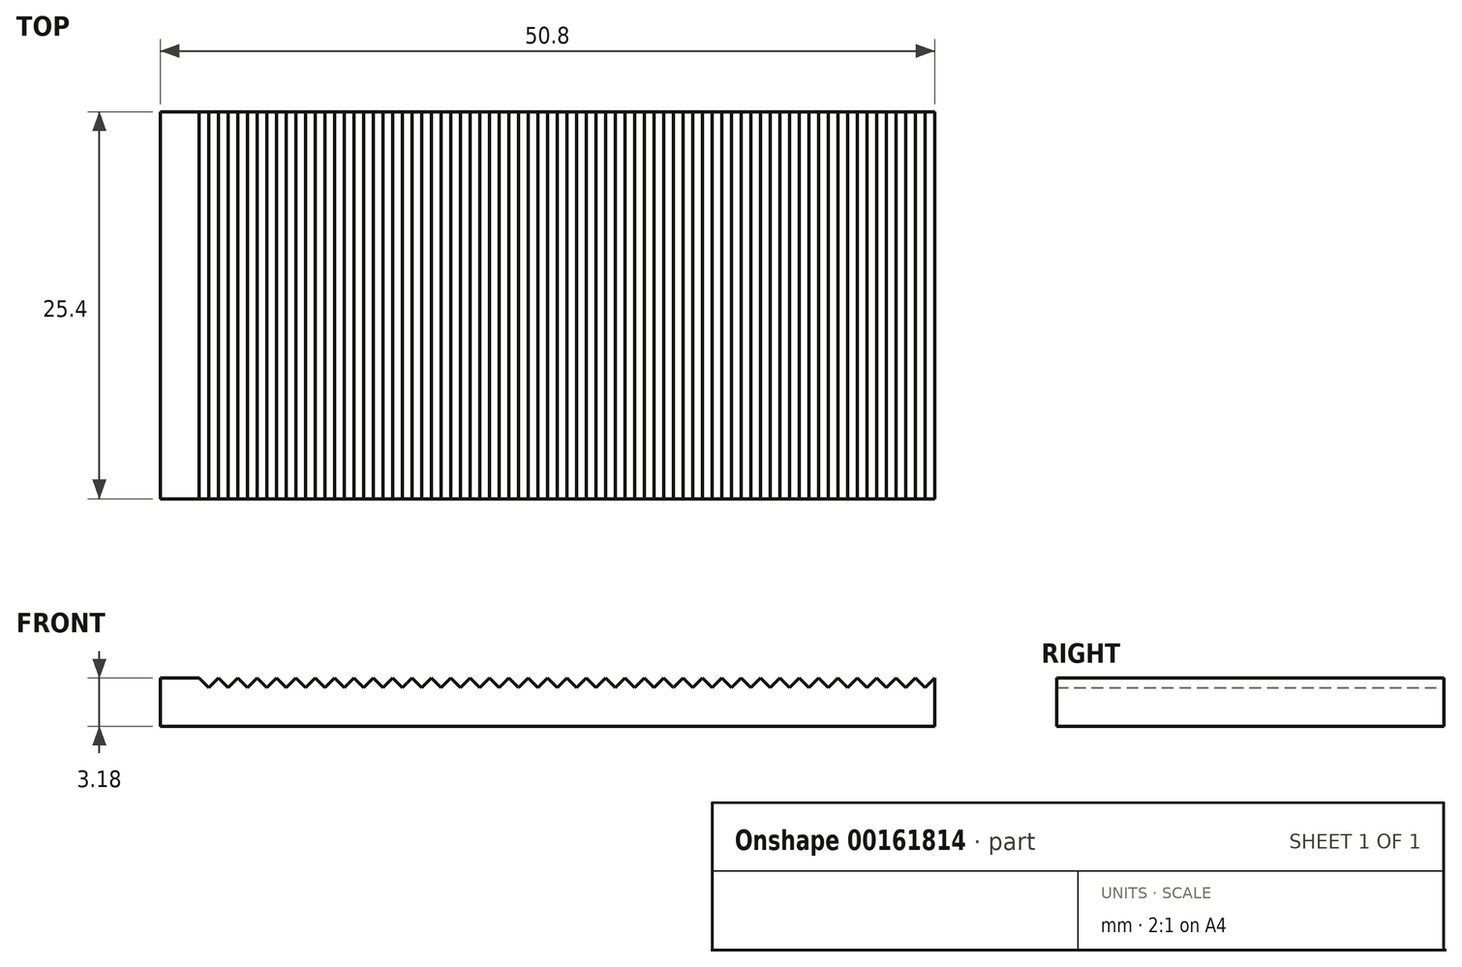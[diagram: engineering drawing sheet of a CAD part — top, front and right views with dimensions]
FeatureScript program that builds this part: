
annotation { "Feature Type Name" : "Feature", "Feature Type Description" : "" }
export const myFeature = defineFeature(function(context is Context, id is Id, definition is map)
    precondition{}
    {
        {
            var Q0;
            Q0=qCreatedBy(makeId("Front.planeOp"), FACE);
            var sketch = newSketch(context, id + "F0", { "sketchPlane" : qUnion([Q0])});
            skLineSegment(sketch, "E0", {"start": v(0, 0) * mm, "end": v(50.8, 0) * mm});
            skLineSegment(sketch, "E1", {"start": v(50.8, 0) * mm, "end": v(50.8, 3.17) * mm});
            skLineSegment(sketch, "E2", {"start": v(50.16, 2.54) * mm, "end": v(49.53, 3.18) * mm});
            skLineSegment(sketch, "E3", {"start": v(50.16, 2.54) * mm, "end": v(50.8, 3.18) * mm});
            skLineSegment(sketch, "E4.1.0.0", {"start": v(48.9, 2.54) * mm, "end": v(49.53, 3.18) * mm});
            skLineSegment(sketch, "E4.1.0.1", {"start": v(48.9, 2.54) * mm, "end": v(48.26, 3.18) * mm});
            skLineSegment(sketch, "E4.2.0.0", {"start": v(47.62, 2.54) * mm, "end": v(48.26, 3.18) * mm});
            skLineSegment(sketch, "E4.2.0.1", {"start": v(47.62, 2.54) * mm, "end": v(47, 3.18) * mm});
            skLineSegment(sketch, "E4.3.0.0", {"start": v(46.35, 2.54) * mm, "end": v(47, 3.18) * mm});
            skLineSegment(sketch, "E4.3.0.1", {"start": v(46.35, 2.54) * mm, "end": v(45.72, 3.18) * mm});
            skLineSegment(sketch, "E4.4.0.0", {"start": v(45.09, 2.54) * mm, "end": v(45.72, 3.18) * mm});
            skLineSegment(sketch, "E4.4.0.1", {"start": v(45.09, 2.54) * mm, "end": v(44.45, 3.18) * mm});
            skLineSegment(sketch, "E4.5.0.0", {"start": v(43.81, 2.54) * mm, "end": v(44.45, 3.18) * mm});
            skLineSegment(sketch, "E4.5.0.1", {"start": v(43.81, 2.54) * mm, "end": v(43.18, 3.18) * mm});
            skLineSegment(sketch, "E4.6.0.0", {"start": v(42.55, 2.54) * mm, "end": v(43.18, 3.18) * mm});
            skLineSegment(sketch, "E4.6.0.1", {"start": v(42.55, 2.54) * mm, "end": v(41.91, 3.18) * mm});
            skLineSegment(sketch, "E4.7.0.0", {"start": v(41.27, 2.54) * mm, "end": v(41.91, 3.18) * mm});
            skLineSegment(sketch, "E4.7.0.1", {"start": v(41.27, 2.54) * mm, "end": v(40.64, 3.18) * mm});
            skLineSegment(sketch, "E4.8.0.0", {"start": v(40, 2.54) * mm, "end": v(40.64, 3.18) * mm});
            skLineSegment(sketch, "E4.8.0.1", {"start": v(40, 2.54) * mm, "end": v(39.37, 3.18) * mm});
            skLineSegment(sketch, "E4.9.0.0", {"start": v(38.73, 2.54) * mm, "end": v(39.37, 3.18) * mm});
            skLineSegment(sketch, "E4.9.0.1", {"start": v(38.73, 2.54) * mm, "end": v(38.1, 3.18) * mm});
            skLineSegment(sketch, "E4.10.0.0", {"start": v(37.46, 2.54) * mm, "end": v(38.1, 3.18) * mm});
            skLineSegment(sketch, "E4.10.0.1", {"start": v(37.46, 2.54) * mm, "end": v(36.83, 3.18) * mm});
            skLineSegment(sketch, "E4.11.0.0", {"start": v(36.2, 2.54) * mm, "end": v(36.83, 3.18) * mm});
            skLineSegment(sketch, "E4.11.0.1", {"start": v(36.2, 2.54) * mm, "end": v(35.56, 3.18) * mm});
            skLineSegment(sketch, "E4.12.0.0", {"start": v(34.92, 2.54) * mm, "end": v(35.56, 3.18) * mm});
            skLineSegment(sketch, "E4.12.0.1", {"start": v(34.92, 2.54) * mm, "end": v(34.3, 3.18) * mm});
            skLineSegment(sketch, "E4.13.0.0", {"start": v(33.65, 2.54) * mm, "end": v(34.3, 3.18) * mm});
            skLineSegment(sketch, "E4.13.0.1", {"start": v(33.65, 2.54) * mm, "end": v(33.02, 3.18) * mm});
            skLineSegment(sketch, "E4.14.0.0", {"start": v(32.38, 2.54) * mm, "end": v(33.02, 3.18) * mm});
            skLineSegment(sketch, "E4.14.0.1", {"start": v(32.38, 2.54) * mm, "end": v(31.75, 3.18) * mm});
            skLineSegment(sketch, "E4.15.0.0", {"start": v(31.11, 2.54) * mm, "end": v(31.75, 3.18) * mm});
            skLineSegment(sketch, "E4.15.0.1", {"start": v(31.11, 2.54) * mm, "end": v(30.48, 3.18) * mm});
            skLineSegment(sketch, "E4.16.0.0", {"start": v(29.84, 2.54) * mm, "end": v(30.48, 3.18) * mm});
            skLineSegment(sketch, "E4.16.0.1", {"start": v(29.84, 2.54) * mm, "end": v(29.21, 3.18) * mm});
            skLineSegment(sketch, "E4.17.0.0", {"start": v(28.57, 2.54) * mm, "end": v(29.21, 3.18) * mm});
            skLineSegment(sketch, "E4.17.0.1", {"start": v(28.57, 2.54) * mm, "end": v(27.94, 3.18) * mm});
            skLineSegment(sketch, "E4.18.0.0", {"start": v(27.3, 2.54) * mm, "end": v(27.94, 3.18) * mm});
            skLineSegment(sketch, "E4.18.0.1", {"start": v(27.3, 2.54) * mm, "end": v(26.67, 3.18) * mm});
            skLineSegment(sketch, "E4.19.0.0", {"start": v(26.03, 2.54) * mm, "end": v(26.67, 3.18) * mm});
            skLineSegment(sketch, "E4.19.0.1", {"start": v(26.03, 2.54) * mm, "end": v(25.4, 3.18) * mm});
            skLineSegment(sketch, "E4.20.0.0", {"start": v(24.76, 2.54) * mm, "end": v(25.4, 3.18) * mm});
            skLineSegment(sketch, "E4.20.0.1", {"start": v(24.76, 2.54) * mm, "end": v(24.13, 3.18) * mm});
            skLineSegment(sketch, "E4.21.0.0", {"start": v(23.5, 2.54) * mm, "end": v(24.13, 3.18) * mm});
            skLineSegment(sketch, "E4.21.0.1", {"start": v(23.5, 2.54) * mm, "end": v(22.86, 3.18) * mm});
            skLineSegment(sketch, "E4.22.0.0", {"start": v(22.22, 2.54) * mm, "end": v(22.86, 3.18) * mm});
            skLineSegment(sketch, "E4.22.0.1", {"start": v(22.22, 2.54) * mm, "end": v(21.6, 3.18) * mm});
            skLineSegment(sketch, "E4.23.0.0", {"start": v(20.95, 2.54) * mm, "end": v(21.59, 3.18) * mm});
            skLineSegment(sketch, "E4.23.0.1", {"start": v(20.95, 2.54) * mm, "end": v(20.32, 3.18) * mm});
            skLineSegment(sketch, "E4.24.0.0", {"start": v(19.68, 2.54) * mm, "end": v(20.32, 3.18) * mm});
            skLineSegment(sketch, "E4.24.0.1", {"start": v(19.68, 2.54) * mm, "end": v(19.05, 3.18) * mm});
            skLineSegment(sketch, "E4.25.0.0", {"start": v(18.41, 2.54) * mm, "end": v(19.05, 3.18) * mm});
            skLineSegment(sketch, "E4.25.0.1", {"start": v(18.41, 2.54) * mm, "end": v(17.78, 3.18) * mm});
            skLineSegment(sketch, "E4.26.0.0", {"start": v(17.14, 2.54) * mm, "end": v(17.78, 3.18) * mm});
            skLineSegment(sketch, "E4.26.0.1", {"start": v(17.14, 2.54) * mm, "end": v(16.51, 3.18) * mm});
            skLineSegment(sketch, "E4.27.0.0", {"start": v(15.87, 2.54) * mm, "end": v(16.5, 3.18) * mm});
            skLineSegment(sketch, "E4.27.0.1", {"start": v(15.87, 2.54) * mm, "end": v(15.24, 3.18) * mm});
            skLineSegment(sketch, "E4.28.0.0", {"start": v(14.6, 2.54) * mm, "end": v(15.24, 3.18) * mm});
            skLineSegment(sketch, "E4.28.0.1", {"start": v(14.6, 2.54) * mm, "end": v(13.97, 3.18) * mm});
            skLineSegment(sketch, "E4.29.0.0", {"start": v(13.33, 2.54) * mm, "end": v(13.97, 3.18) * mm});
            skLineSegment(sketch, "E4.29.0.1", {"start": v(13.33, 2.54) * mm, "end": v(12.7, 3.18) * mm});
            skLineSegment(sketch, "E4.30.0.0", {"start": v(12.06, 2.54) * mm, "end": v(12.7, 3.18) * mm});
            skLineSegment(sketch, "E4.30.0.1", {"start": v(12.06, 2.54) * mm, "end": v(11.43, 3.18) * mm});
            skLineSegment(sketch, "E4.31.0.0", {"start": v(10.8, 2.54) * mm, "end": v(11.43, 3.18) * mm});
            skLineSegment(sketch, "E4.31.0.1", {"start": v(10.8, 2.54) * mm, "end": v(10.16, 3.18) * mm});
            skLineSegment(sketch, "E4.32.0.0", {"start": v(9.52, 2.54) * mm, "end": v(10.16, 3.18) * mm});
            skLineSegment(sketch, "E4.32.0.1", {"start": v(9.52, 2.54) * mm, "end": v(8.89, 3.18) * mm});
            skLineSegment(sketch, "E4.33.0.0", {"start": v(8.25, 2.54) * mm, "end": v(8.89, 3.18) * mm});
            skLineSegment(sketch, "E4.33.0.1", {"start": v(8.25, 2.54) * mm, "end": v(7.62, 3.18) * mm});
            skLineSegment(sketch, "E4.34.0.0", {"start": v(6.98, 2.54) * mm, "end": v(7.62, 3.18) * mm});
            skLineSegment(sketch, "E4.34.0.1", {"start": v(6.98, 2.54) * mm, "end": v(6.35, 3.18) * mm});
            skLineSegment(sketch, "E4.35.0.0", {"start": v(5.71, 2.54) * mm, "end": v(6.35, 3.18) * mm});
            skLineSegment(sketch, "E4.35.0.1", {"start": v(5.71, 2.54) * mm, "end": v(5.08, 3.18) * mm});
            skLineSegment(sketch, "E4.36.0.0", {"start": v(4.44, 2.54) * mm, "end": v(5.08, 3.18) * mm});
            skLineSegment(sketch, "E4.36.0.1", {"start": v(4.44, 2.54) * mm, "end": v(3.8, 3.18) * mm});
            skLineSegment(sketch, "E4.37.0.0", {"start": v(3.17, 2.54) * mm, "end": v(3.8, 3.18) * mm});
            skLineSegment(sketch, "E4.37.0.1", {"start": v(3.17, 2.54) * mm, "end": v(2.54, 3.18) * mm});
            skLineSegment(sketch, "E4.direction1", {"start": v(50.16, 2.54) * mm, "end": v(48.9, 2.54) * mm, "construction": true});
            skLineSegment(sketch, "E5", {"start": v(0, 3.17) * mm, "end": v(2.54, 3.17) * mm});
            skLineSegment(sketch, "E6", {"start": v(0, 3.17) * mm, "end": v(0, 0) * mm});
            skSolve(sketch);
        }
        {
            var Q0;
            Q0 = qSketchRegion(id + "F0", true);
            extrude(context, id + "F1", {"entities" : qUnion([Q0]), "depth" : 25.4 * mm, "offsetDistance" : 25.4 * mm});
        }
    });
